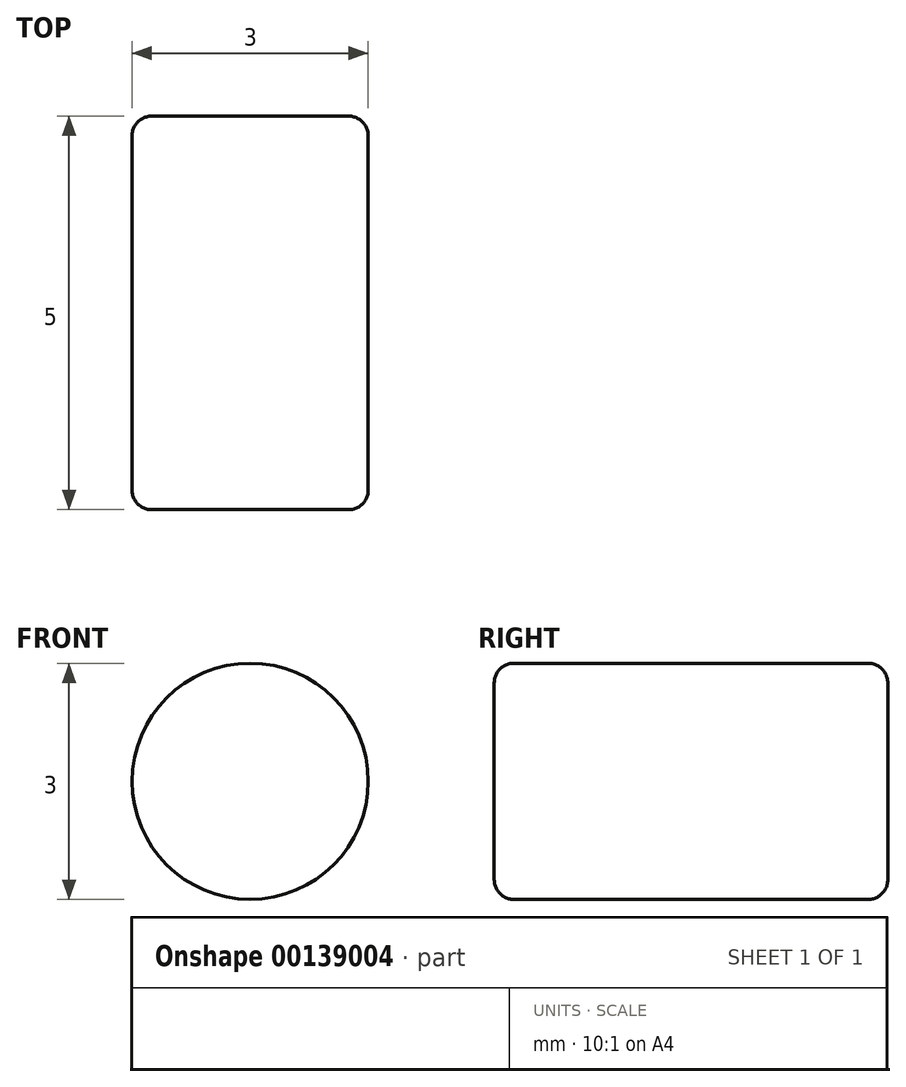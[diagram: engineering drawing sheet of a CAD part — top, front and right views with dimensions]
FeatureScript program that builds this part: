
annotation { "Feature Type Name" : "Feature", "Feature Type Description" : "" }
export const myFeature = defineFeature(function(context is Context, id is Id, definition is map)
    precondition{}
    {
        {
            var Q0;
            Q0=qCreatedBy(makeId("Front.planeOp"),FACE);
            var sketch = newSketch(context, id + "F0", { "sketchPlane" : qUnion([Q0])});
            skCircle(sketch, "E0", {"center": v(0, 0) * mm, "radius": 1.5 * mm});
            skSolve(sketch);
        }
        {
            var Q0;
            Q0 = qSketchRegion(id + "F0", true);
            extrude(context, id + "F1", {"entities" : qUnion([Q0]), "depth" : 5 * mm});
        }
        {
            var Q0;
            Q0=makeQuery(id+"F1.opExtrude","CAP_EDGE",EDGE,{"disambiguationData":[OSD([sQuery(id+"F0.wireOp",EDGE,"E0")])],"isStart":false});
            var Q1;
            Q1=makeQuery(id+"F1.opExtrude","CAP_EDGE",EDGE,{"disambiguationData":[OSD([sQuery(id+"F0.wireOp",EDGE,"E0")])],"isStart":true});
            fillet(context, id + "F2", {"entities" : qUnion([Q0, Q1]), "radius" : .25 * mm, "tangentPropagation" : true, "allowEdgeOverflow" : false});
        }
    });
